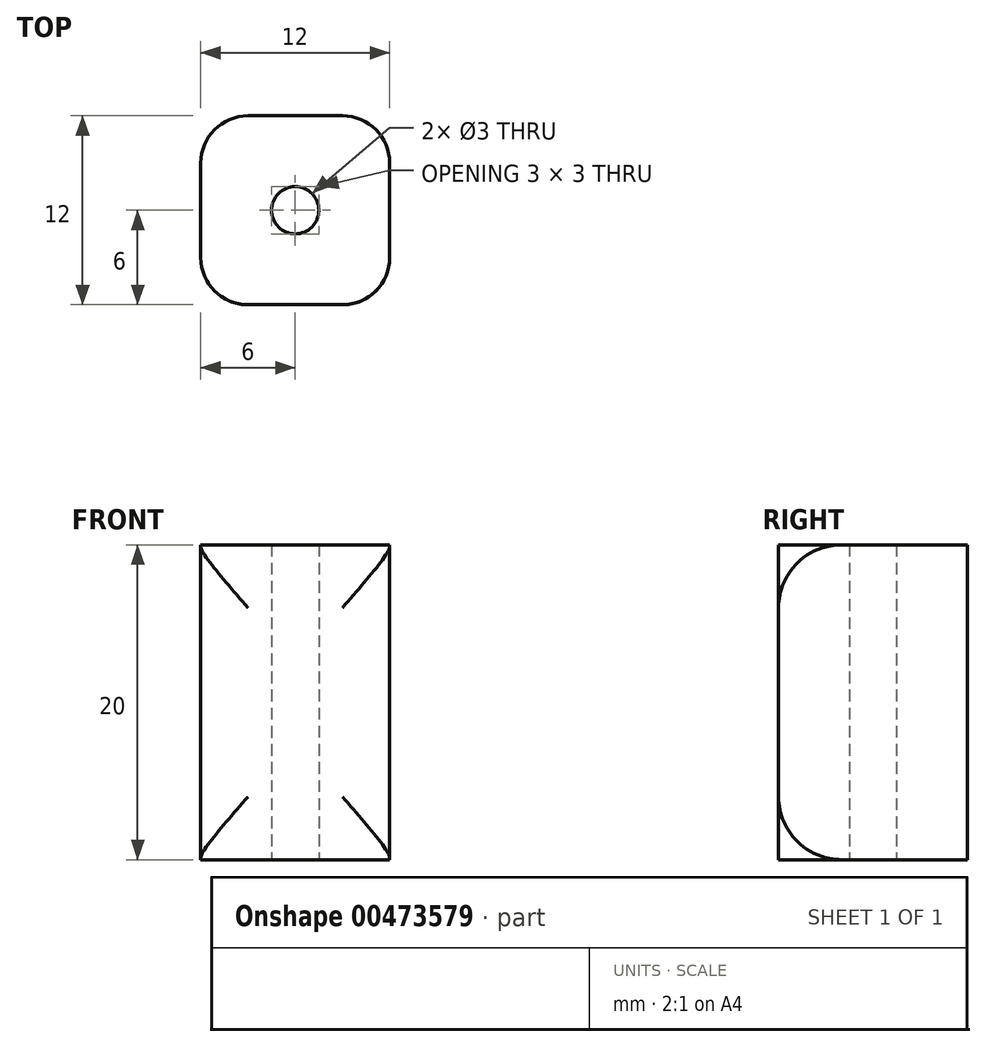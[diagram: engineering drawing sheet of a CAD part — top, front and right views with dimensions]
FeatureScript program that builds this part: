
annotation { "Feature Type Name" : "Feature", "Feature Type Description" : "" }
export const myFeature = defineFeature(function(context is Context, id is Id, definition is map)
    precondition{}
    {
        {
            var Q0;
            Q0=qCreatedBy(makeId("Top.planeOp"),FACE);
            var sketch = newSketch(context, id + "F0", { "sketchPlane" : qUnion([Q0])});
            skLineSegment(sketch, "E0.bottom", {"start": v(3, 6) * mm, "end": v(-3, 6) * mm});
            skLineSegment(sketch, "E0.top", {"start": v(3, -6) * mm, "end": v(-3, -6) * mm});
            skLineSegment(sketch, "E0.left", {"start": v(6, 3) * mm, "end": v(6, -3) * mm});
            skLineSegment(sketch, "E0.right", {"start": v(-6, 3) * mm, "end": v(-6, -3) * mm});
            skPoint(sketch, "E0.middle", {"position": v(0, 0) * mm});
            skPoint(sketch, "E1.visualSharp", {"position": v(-6, 6) * mm});
            skArc(sketch, "E1.filletArc", {"start": v(-3, 6) * mm, "mid": v(-5.12, 5.12) * mm, "end": v(-6, 3) * mm});
            skPoint(sketch, "E2.visualSharp", {"position": v(6, 6) * mm});
            skArc(sketch, "E2.filletArc", {"start": v(6, 3) * mm, "mid": v(5.12, 5.12) * mm, "end": v(3, 6) * mm});
            skPoint(sketch, "E3.visualSharp", {"position": v(6, -6) * mm});
            skArc(sketch, "E3.filletArc", {"start": v(3, -6) * mm, "mid": v(5.12, -5.12) * mm, "end": v(6, -3) * mm});
            skPoint(sketch, "E4.visualSharp", {"position": v(-6, -6) * mm});
            skArc(sketch, "E4.filletArc", {"start": v(-6, -3) * mm, "mid": v(-5.12, -5.12) * mm, "end": v(-3, -6) * mm});
            skSolve(sketch);
        }
        {
            var Q0;
            Q0=makeQuery(id+"F0.imprint","IMPRINT",FACE,{"disambiguationData":[TD([[makeQuery(id+"F0.imprint","IMPRINT",EDGE,{"derivedFrom":sQuery(id+"F0.wireOp",EDGE,"E0.bottom")}),1.0]])]});
            extrude(context, id + "F1", {"entities" : qUnion([Q0]), "depth" : 20 * mm});
        }
        {
            var Q0;
            Q0=makeQuery(id+"F0.imprint","IMPRINT",FACE,{"disambiguationData":[TD([[makeQuery(id+"F0.imprint","IMPRINT",EDGE,{"derivedFrom":sQuery(id+"F0.wireOp",EDGE,"E0.bottom")}),1.0]])]});
            extrude(context, id + "F2", {"entities" : qUnion([Q0]), "depth" : 20 * mm});
        }
        {
            var Q0;
            Q0=makeQuery(id+"F2.opExtrude","CAP_EDGE",EDGE,{"disambiguationData":[OSD([sQuery(id+"F0.wireOp",EDGE,"E0.top")])],"isStart":false});
            var Q1;
            Q1=makeQuery(id+"F2.opExtrude","CAP_EDGE",EDGE,{"disambiguationData":[OSD([sQuery(id+"F0.wireOp",EDGE,"E0.top")])],"isStart":true});
            fillet(context, id + "F3", {"entities" : qUnion([Q0, Q1]), "radius" : 4 * mm, "allowEdgeOverflow" : false});
        }
        {
            var Q0;
            Q0=sQuery(id+"F0.wireOp",VERTEX,"E0.middle");
            var Q1;
            Q1=makeQuery(id+"F2.opExtrude","SWEPT_BODY",BODY,{"disambiguationData":[OSD([sQuery(id+"F0.wireOp",EDGE,"E0.bottom"),sQuery(id+"F0.wireOp",EDGE,"E0.top"),sQuery(id+"F0.wireOp",EDGE,"E0.left"),sQuery(id+"F0.wireOp",EDGE,"E0.right"),sQuery(id+"F0.wireOp",EDGE,"E1.filletArc"),sQuery(id+"F0.wireOp",EDGE,"E2.filletArc"),sQuery(id+"F0.wireOp",EDGE,"E3.filletArc"),sQuery(id+"F0.wireOp",EDGE,"E4.filletArc")])]});
            var Q2;
            Q2=makeQuery(id+"F1.opExtrude","SWEPT_BODY",BODY,{"disambiguationData":[OSD([sQuery(id+"F0.wireOp",EDGE,"E0.bottom"),sQuery(id+"F0.wireOp",EDGE,"E0.top"),sQuery(id+"F0.wireOp",EDGE,"E0.left"),sQuery(id+"F0.wireOp",EDGE,"E0.right"),sQuery(id+"F0.wireOp",EDGE,"E1.filletArc"),sQuery(id+"F0.wireOp",EDGE,"E2.filletArc"),sQuery(id+"F0.wireOp",EDGE,"E3.filletArc"),sQuery(id+"F0.wireOp",EDGE,"E4.filletArc")])]});
            hole(context, id + "F4", {"style" : HoleStyle.SIMPLE, "endStyle" : HoleEndStyle.THROUGH, "oppositeDirection" : true, "holeDiameter" : 3 * mm, "isTappedThrough" : true, "tappedDepth" : 12 * mm, "tapClearance" : 3, "locations" : qUnion([Q0]), "scope" : qUnion([Q1, Q2])});
        }
    });
